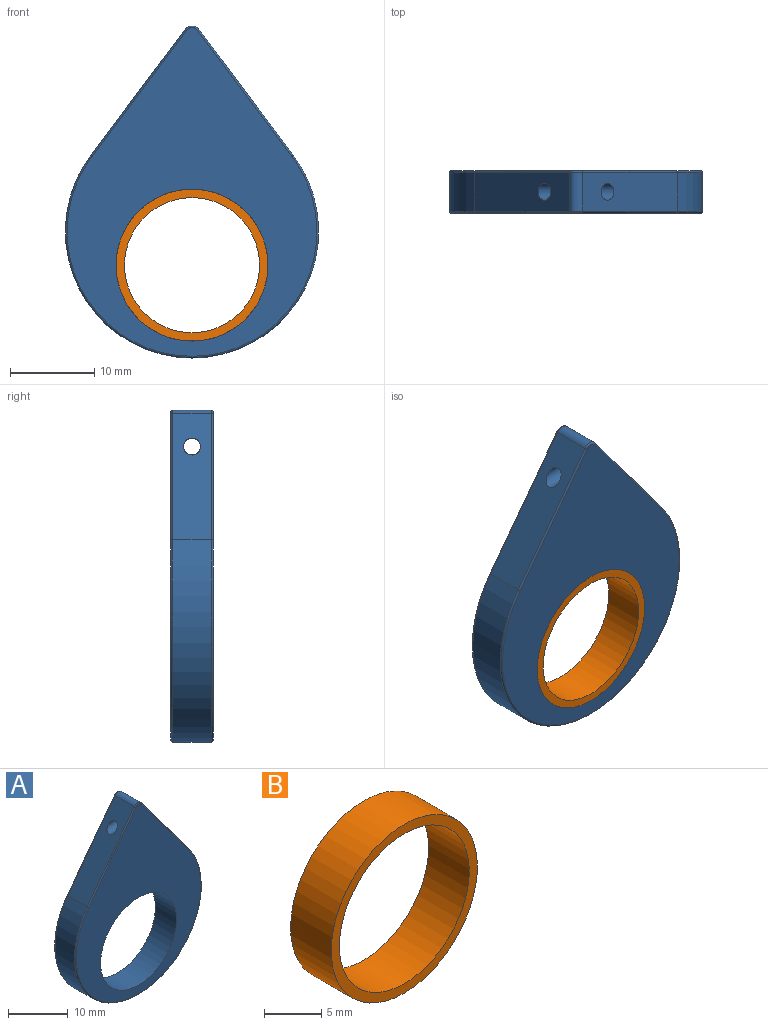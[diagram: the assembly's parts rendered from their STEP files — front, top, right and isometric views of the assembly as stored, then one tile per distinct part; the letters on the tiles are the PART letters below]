
ASSEMBLY  parts=2 mates=1
PART A: 16 faces, bbox 32.8x5.3x41 mm
  f0: plane 14.93x11.2mm, normal (0.8,0,0.6), area 81.9mm2, adj f5,f6,f7,f11,f15
  f1: plane 38.93x29.6mm, normal (0,-1,0), area 522.3mm2, adj f3,f8,f9,f10,f11
  f2: plane 38.93x29.6mm, normal (0,1,0), area 522.3mm2, adj f3,f12,f13,f14,f15
  f3: cylinder r=9mm len=18mm, axis (0,-1,0), area 282.7mm2, adj f1,f2
  f4: plane 15.25x11.52mm, normal (-0.8,0,0.6), area 81.9mm2, adj f5,f6,f7,f8,f12
  f5: cylinder r=1mm len=4.6mm, axis (0,1,0), area 8.5mm2, adj f0,f4,f9,f13
  f6: cylinder r=1mm len=9mm, axis (1,0,0), area 47.1mm2, adj f0,f4
  f7: cylinder r=15mm len=30mm, axis (0,1,0), area 305.6mm2, adj f0,f4,f10,f14
  f8: cylinder r=0.2mm len=15.05mm, axis (-0.6,0,-0.8), area 5.9mm2, adj f1,f4,f9,f10
  f9: torus R=0.8mm, axis (0,-1,0), area 0.5mm2, adj f1,f5,f8,f11
  f10: torus R=14.8mm, axis (0,-1,0), area 20.8mm2, adj f1,f7,f8,f11
  f11: cylinder r=0.2mm len=15.05mm, axis (0.6,0,-0.8), area 5.9mm2, adj f0,f1,f9,f10
  f12: cylinder r=0.2mm len=15.05mm, axis (0.6,0,0.8), area 5.9mm2, adj f2,f4,f13,f14
  f13: torus R=0.8mm, axis (0,-1,0), area 0.5mm2, adj f2,f5,f12,f15
  f14: torus R=14.8mm, axis (0,-1,0), area 20.8mm2, adj f2,f7,f12,f15
  f15: cylinder r=0.2mm len=15.05mm, axis (-0.6,0,0.8), area 5.9mm2, adj f0,f2,f13,f14
PART B: 4 faces, bbox 18x5x18 mm
  f0: cylinder r=8mm len=16mm, axis (0,1,0), area 251.3mm2, adj f2,f3
  f1: cylinder r=9mm len=18mm, axis (0,1,0), area 282.7mm2, adj f2,f3
  f2: plane 18x18mm, normal (0,-1,0), area 53.4mm2, adj f0,f1
  f3: plane 18x18mm, normal (0,1,0), area 53.4mm2, adj f0,f1
PLACE A t=(-0.04,3.45,-13.14)mm fixed
PLACE B rot(axis=(0,-1,0),180deg) t=(-0.04,3.45,-2.14)mm
MATE fastened A.f3 <-> B.f1  axis (0,-1,0) through (-0.04,0.95,-2.14)mm
